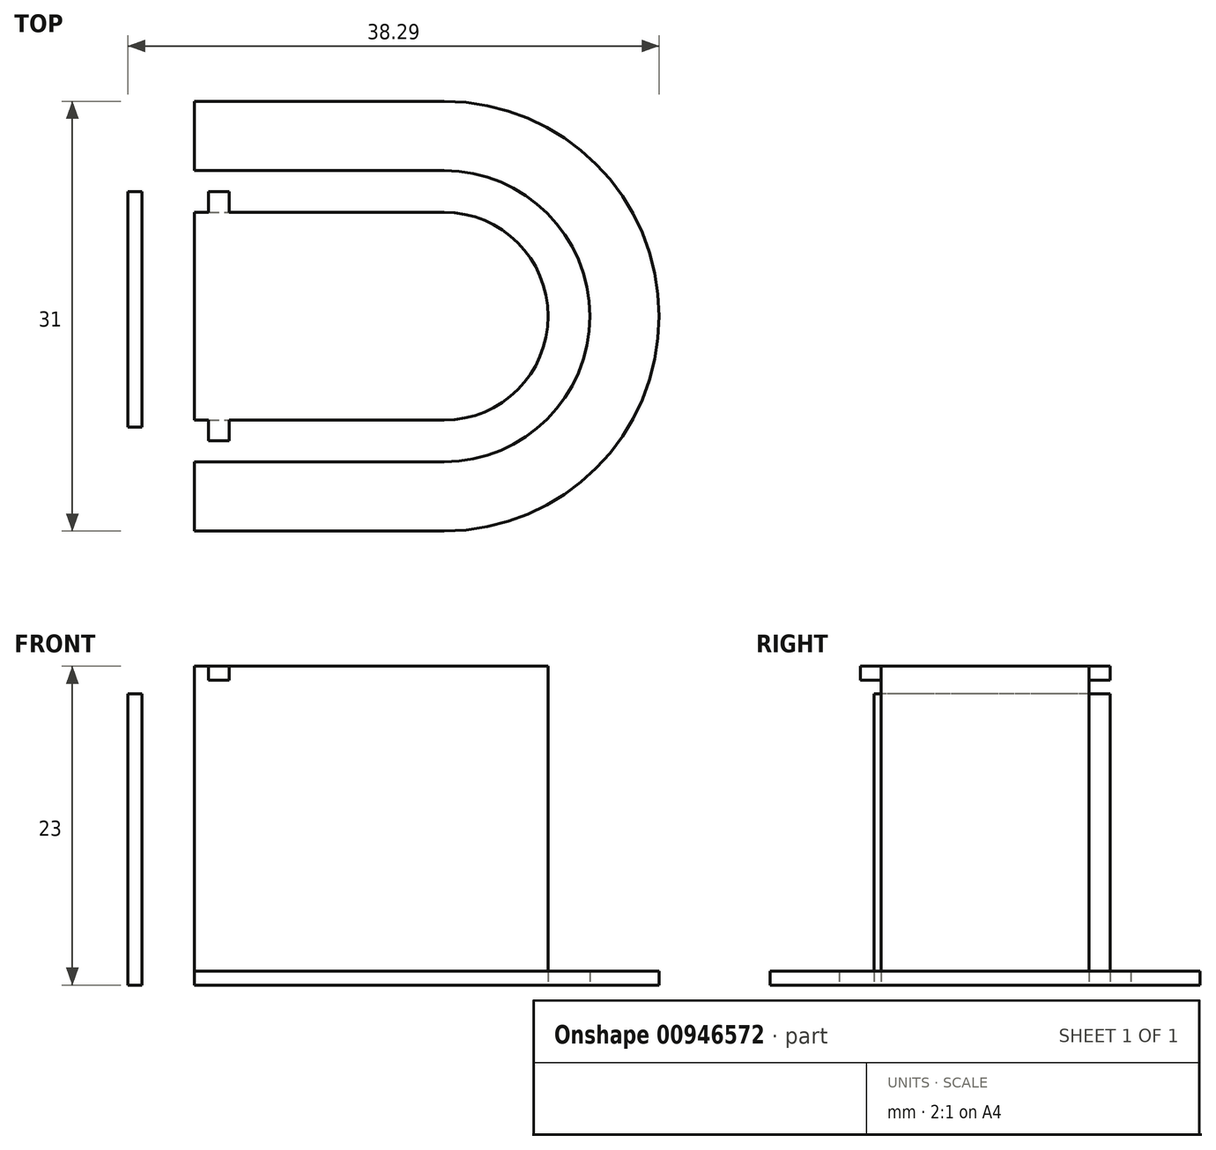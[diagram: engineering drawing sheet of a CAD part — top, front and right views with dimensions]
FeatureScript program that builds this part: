
annotation { "Feature Type Name" : "Feature", "Feature Type Description" : "" }
export const myFeature = defineFeature(function(context is Context, id is Id, definition is map)
    precondition{}
    {
        {
            var Q0;
            Q0=qCreatedBy(makeId("Top.planeOp"),FACE);
            var sketch = newSketch(context, id + "F0", { "sketchPlane" : qUnion([Q0])});
            skLineSegment(sketch, "E0.bottom", {"start": v(-45.57, 29.39) * mm, "end": v(-27.57, 29.39) * mm});
            skLineSegment(sketch, "E0.top", {"start": v(-45.57, 14.39) * mm, "end": v(-27.57, 14.39) * mm});
            skLineSegment(sketch, "E0.left", {"start": v(-45.57, 29.39) * mm, "end": v(-45.57, 14.39) * mm});
            skArc(sketch, "E1", {"start": v(-27.57, 29.39) * mm, "mid": v(-20.07, 21.89) * mm, "end": v(-27.57, 14.39) * mm});
            skLineSegment(sketch, "E2.0", {"start": v(-45.57, 6.39) * mm, "end": v(-27.57, 6.39) * mm});
            skArc(sketch, "E2.1", {"start": v(-27.57, 37.39) * mm, "mid": v(-12.07, 21.89) * mm, "end": v(-27.57, 6.39) * mm});
            skLineSegment(sketch, "E2.2", {"start": v(-45.57, 37.39) * mm, "end": v(-27.57, 37.39) * mm});
            skLineSegment(sketch, "E3", {"start": v(-45.57, 29.39) * mm, "end": v(-45.57, 37.39) * mm});
            skLineSegment(sketch, "E4", {"start": v(-45.57, 14.39) * mm, "end": v(-45.57, 6.39) * mm});
            skLineSegment(sketch, "E5.0", {"start": v(-45.57, 11.39) * mm, "end": v(-27.57, 11.39) * mm});
            skArc(sketch, "E5.1", {"start": v(-27.57, 32.39) * mm, "mid": v(-17.07, 21.89) * mm, "end": v(-27.57, 11.39) * mm});
            skLineSegment(sketch, "E5.2", {"start": v(-45.57, 32.39) * mm, "end": v(-27.57, 32.39) * mm});
            skLineSegment(sketch, "E6.bottom", {"start": v(-44.54, 29.39) * mm, "end": v(-43.04, 29.39) * mm});
            skLineSegment(sketch, "E6.top", {"start": v(-44.54, 30.89) * mm, "end": v(-43.04, 30.89) * mm});
            skLineSegment(sketch, "E6.left", {"start": v(-44.54, 29.39) * mm, "end": v(-44.54, 30.89) * mm});
            skLineSegment(sketch, "E6.right", {"start": v(-43.04, 29.39) * mm, "end": v(-43.04, 30.89) * mm});
            skLineSegment(sketch, "E7.bottom", {"start": v(-44.54, 14.39) * mm, "end": v(-43.04, 14.39) * mm});
            skLineSegment(sketch, "E7.top", {"start": v(-44.54, 12.89) * mm, "end": v(-43.04, 12.89) * mm});
            skLineSegment(sketch, "E7.left", {"start": v(-44.54, 14.39) * mm, "end": v(-44.54, 12.89) * mm});
            skLineSegment(sketch, "E7.right", {"start": v(-43.04, 14.39) * mm, "end": v(-43.04, 12.89) * mm});
            skLineSegment(sketch, "E8.bottom", {"start": v(-49.36, 30.89) * mm, "end": v(-50.36, 30.89) * mm});
            skLineSegment(sketch, "E8.top", {"start": v(-49.36, 13.89) * mm, "end": v(-50.36, 13.89) * mm});
            skLineSegment(sketch, "E8.left", {"start": v(-49.36, 30.89) * mm, "end": v(-49.36, 13.89) * mm});
            skLineSegment(sketch, "E8.right", {"start": v(-50.36, 30.89) * mm, "end": v(-50.36, 13.89) * mm});
            skSolve(sketch);
        }
        {
            var Q0;
            {var subQ3=sQuery(id+"F0.wireOp",EDGE,"E2.0");Q0=makeQuery(id+"F0.imprint","IMPRINT",FACE,{"disambiguationData":[TD([[makeQuery(id+"F0.imprint","IMPRINT",EDGE,{"derivedFrom":subQ3}),1.0]])]});}
            extrude(context, id + "F1", {"entities" : qUnion([Q0]), "depth" : 1 * mm, "offsetDistance" : 25 * mm});
        }
        {
            var Q0;
            {var subQ6=sQuery(id+"F0.wireOp",EDGE,"E1");Q0=makeQuery(id+"F0.imprint","IMPRINT",FACE,{"disambiguationData":[TD([[makeQuery(id+"F0.imprint","IMPRINT",EDGE,{"derivedFrom":subQ6}),1.0]])]});}
            extrude(context, id + "F2", {"entities" : qUnion([Q0]), "operationType" : NewBodyOperationType.ADD, "depth" : 23 * mm, "offsetDistance" : 25 * mm});
        }
        {
            var Q0;
            Q0=makeQuery(id+"F0.imprint","IMPRINT",FACE,{"disambiguationData":[TD([[makeQuery(id+"F0.imprint","IMPRINT",EDGE,{"derivedFrom":sQuery(id+"F0.wireOp",EDGE,"E6.top")}),-1.0]])]});
            var Q1;
            Q1=makeQuery(id+"F0.imprint","IMPRINT",FACE,{"disambiguationData":[TD([[makeQuery(id+"F0.imprint","IMPRINT",EDGE,{"derivedFrom":sQuery(id+"F0.wireOp",EDGE,"E7.top")}),1.0]])]});
            extrude(context, id + "F3", {"entities" : qUnion([Q0, Q1]), "operationType" : NewBodyOperationType.ADD, "depth" : 23 * mm, "offsetDistance" : 25 * mm, "hasSecondDirection" : true, "secondDirectionOppositeDirection" : false, "secondDirectionDepth" : 22 * mm});
        }
        {
            var Q0;
            Q0=makeQuery(id+"F0.imprint","IMPRINT",FACE,{"disambiguationData":[TD([[makeQuery(id+"F0.imprint","IMPRINT",EDGE,{"derivedFrom":sQuery(id+"F0.wireOp",EDGE,"E8.bottom")}),1.0]])]});
            extrude(context, id + "F4", {"entities" : qUnion([Q0]), "depth" : 21 * mm, "offsetDistance" : 25 * mm});
        }
    });
